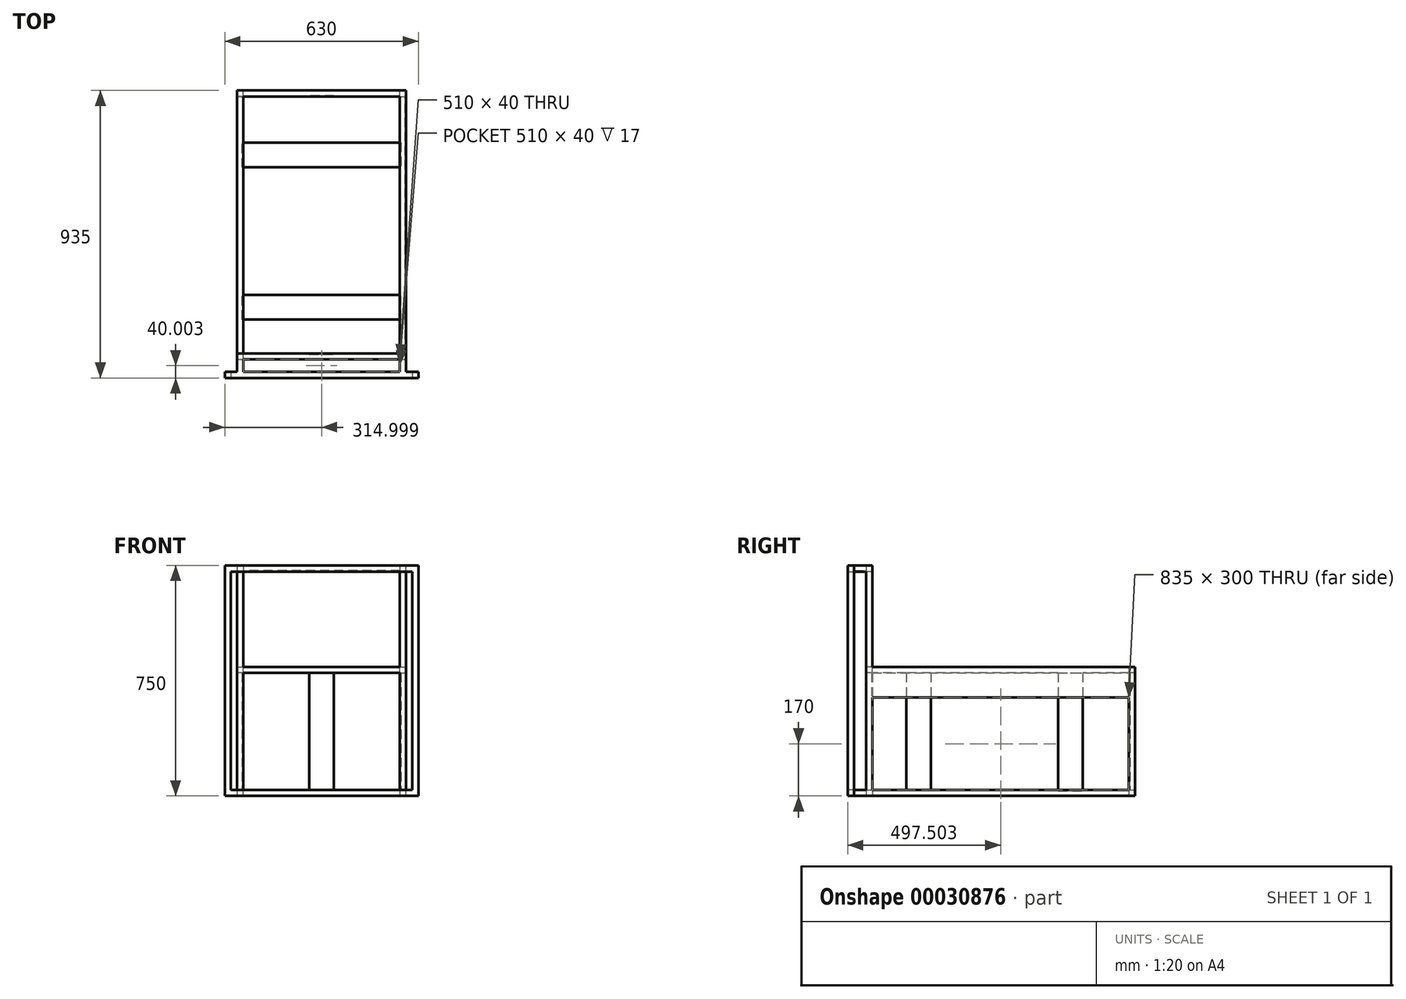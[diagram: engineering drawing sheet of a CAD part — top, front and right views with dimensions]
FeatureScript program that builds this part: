
annotation { "Feature Type Name" : "Feature", "Feature Type Description" : "" }
export const myFeature = defineFeature(function(context is Context, id is Id, definition is map)
    precondition{}
    {
        {
            var Q0;
            Q0=qCreatedBy(makeId("Top.planeOp"),FACE);
            var sketch = newSketch(context, id + "F0", { "sketchPlane" : qUnion([Q0])});
            skLineSegment(sketch, "E0.bottom", {"start": v(-142.85, 483.07) * mm, "end": v(407.15, 483.07) * mm});
            skLineSegment(sketch, "E0.top", {"start": v(-142.85, -391.93) * mm, "end": v(407.15, -391.93) * mm});
            skLineSegment(sketch, "E0.left", {"start": v(-142.85, 483.07) * mm, "end": v(-142.85, -391.93) * mm});
            skLineSegment(sketch, "E0.right", {"start": v(407.15, 483.07) * mm, "end": v(407.15, -391.93) * mm});
            skSolve(sketch);
        }
        {
            var Q0;
            Q0 = qSketchRegion(id + "F0", true);
            extrude(context, id + "F1", {"entities" : qUnion([Q0]), "depth" : 20 * mm});
        }
        {
            var Q0;
            Q0=makeQuery(id+"F1.opExtrude","CAP_FACE",FACE,{"disambiguationData":[OSD([sQuery(id+"F0.wireOp",EDGE,"E0.bottom"),sQuery(id+"F0.wireOp",EDGE,"E0.top"),sQuery(id+"F0.wireOp",EDGE,"E0.left"),sQuery(id+"F0.wireOp",EDGE,"E0.right")])],"isStart":true});
            var sketch = newSketch(context, id + "F2", { "sketchPlane" : qUnion([Q0])});
            skLineSegment(sketch, "E1.bottom", {"start": v(-122.85, 371.93) * mm, "end": v(387.15, 371.93) * mm});
            skLineSegment(sketch, "E1.top", {"start": v(-122.85, -463.07) * mm, "end": v(387.15, -463.07) * mm});
            skLineSegment(sketch, "E1.left", {"start": v(-122.85, 371.93) * mm, "end": v(-122.85, -463.07) * mm});
            skLineSegment(sketch, "E1.right", {"start": v(387.15, 371.93) * mm, "end": v(387.15, -463.07) * mm});
            skSolve(sketch);
        }
        {
            var Q0;
            Q0 = qSketchRegion(id + "F2", true);
            extrude(context, id + "F3", {"entities" : qUnion([Q0]), "operationType" : NewBodyOperationType.REMOVE, "endBound" : BoundingType.THROUGH_ALL, "oppositeDirection" : true, "depth" : 21 * mm});
        }
        {
            var Q0;
            Q0=makeQuery(id+"F3.boolean.opBoolean","COPY",FACE,{"derivedFrom":makeQuery(id+"F3.opExtrude","SWEPT_FACE",FACE,{"disambiguationData":[OSD([sQuery(id+"F2.wireOp",EDGE,"E1.left")])]})});
            var sketch = newSketch(context, id + "F4", { "sketchPlane" : qUnion([Q0])});
            skLineSegment(sketch, "E2.bottom", {"start": v(313.07, 20) * mm, "end": v(233.07, 20) * mm});
            skLineSegment(sketch, "E2.top", {"start": v(313.07, 17) * mm, "end": v(233.07, 17) * mm});
            skLineSegment(sketch, "E2.left", {"start": v(313.07, 20) * mm, "end": v(313.07, 17) * mm});
            skLineSegment(sketch, "E2.right", {"start": v(233.07, 20) * mm, "end": v(233.07, 17) * mm});
            skLineSegment(sketch, "E3.bottom", {"start": v(-261.93, 20) * mm, "end": v(-181.93, 20) * mm});
            skLineSegment(sketch, "E3.top", {"start": v(-261.93, 17) * mm, "end": v(-181.93, 17) * mm});
            skLineSegment(sketch, "E3.left", {"start": v(-261.93, 20) * mm, "end": v(-261.93, 17) * mm});
            skLineSegment(sketch, "E3.right", {"start": v(-181.93, 20) * mm, "end": v(-181.93, 17) * mm});
            skSolve(sketch);
        }
        {
            var Q0;
            Q0 = qSketchRegion(id + "F4", true);
            extrude(context, id + "F5", {"entities" : qUnion([Q0]), "operationType" : NewBodyOperationType.ADD, "endBound" : BoundingType.UP_TO_NEXT, "depth" : 25 * mm});
        }
        {
            var Q0;
            Q0=makeQuery(id+"F5.boolean.opBoolean","MERGE",FACE,{"derivedFrom":[makeQuery(id+"F1.opExtrude","CAP_FACE",FACE,{"disambiguationData":[OSD([sQuery(id+"F0.wireOp",EDGE,"E0.bottom"),sQuery(id+"F0.wireOp",EDGE,"E0.top"),sQuery(id+"F0.wireOp",EDGE,"E0.left"),sQuery(id+"F0.wireOp",EDGE,"E0.right")])],"isStart":false}),makeQuery(id+"F5.opExtrude","SWEPT_FACE",FACE,{"disambiguationData":[OSD([sQuery(id+"F4.wireOp",EDGE,"70eb4137-1e62-4804-9132-5afcea929224.bottom")])]}),makeQuery(id+"F5.opExtrude","SWEPT_FACE",FACE,{"disambiguationData":[OSD([sQuery(id+"F4.wireOp",EDGE,"E2.bottom")])]})]});
            var sketch = newSketch(context, id + "F6", { "sketchPlane" : qUnion([Q0])});
            skLineSegment(sketch, "E4.bottom", {"start": v(-142.85, -391.93) * mm, "end": v(-122.85, -391.93) * mm});
            skLineSegment(sketch, "E4.top", {"start": v(-142.85, -371.93) * mm, "end": v(-122.85, -371.93) * mm});
            skLineSegment(sketch, "E4.left", {"start": v(-142.85, -391.93) * mm, "end": v(-142.85, -371.93) * mm});
            skLineSegment(sketch, "E4.right", {"start": v(-122.85, -391.93) * mm, "end": v(-122.85, -371.93) * mm});
            skLineSegment(sketch, "E5.bottom", {"start": v(407.15, -391.93) * mm, "end": v(387.15, -391.93) * mm});
            skLineSegment(sketch, "E5.top", {"start": v(407.15, -371.93) * mm, "end": v(387.15, -371.93) * mm});
            skLineSegment(sketch, "E5.left", {"start": v(407.15, -391.93) * mm, "end": v(407.15, -371.93) * mm});
            skLineSegment(sketch, "E5.right", {"start": v(387.15, -391.93) * mm, "end": v(387.15, -371.93) * mm});
            skLineSegment(sketch, "E6.bottom", {"start": v(-122.85, 463.07) * mm, "end": v(-142.85, 463.07) * mm});
            skLineSegment(sketch, "E6.top", {"start": v(-122.85, 483.07) * mm, "end": v(-142.85, 483.07) * mm});
            skLineSegment(sketch, "E6.left", {"start": v(-122.85, 463.07) * mm, "end": v(-122.85, 483.07) * mm});
            skLineSegment(sketch, "E6.right", {"start": v(-142.85, 463.07) * mm, "end": v(-142.85, 483.07) * mm});
            skLineSegment(sketch, "E7.bottom", {"start": v(387.15, 463.07) * mm, "end": v(407.15, 463.07) * mm});
            skLineSegment(sketch, "E7.top", {"start": v(387.15, 483.07) * mm, "end": v(407.15, 483.07) * mm});
            skLineSegment(sketch, "E7.left", {"start": v(387.15, 463.07) * mm, "end": v(387.15, 483.07) * mm});
            skLineSegment(sketch, "E7.right", {"start": v(407.15, 463.07) * mm, "end": v(407.15, 483.07) * mm});
            skSolve(sketch);
        }
        {
            var Q0;
            Q0 = qSketchRegion(id + "F6", true);
            extrude(context, id + "F7", {"entities" : qUnion([Q0]), "depth" : 400 * mm});
        }
        {
            var Q0;
            Q0=makeQuery(id+"F7.opExtrude","SWEPT_FACE",FACE,{"disambiguationData":[OSD([sQuery(id+"F6.wireOp",EDGE,"E5.top")])]});
            var sketch = newSketch(context, id + "F8", { "sketchPlane" : qUnion([Q0])});
            skLineSegment(sketch, "E8.bottom", {"start": v(-387.15, 420) * mm, "end": v(-407.15, 420) * mm});
            skLineSegment(sketch, "E8.top", {"start": v(-387.15, 400) * mm, "end": v(-407.15, 400) * mm});
            skLineSegment(sketch, "E8.left", {"start": v(-387.15, 420) * mm, "end": v(-387.15, 400) * mm});
            skLineSegment(sketch, "E8.right", {"start": v(-407.15, 420) * mm, "end": v(-407.15, 400) * mm});
            skSolve(sketch);
        }
        {
            var Q0;
            Q0 = qSketchRegion(id + "F8", true);
            extrude(context, id + "F9", {"entities" : qUnion([Q0]), "operationType" : NewBodyOperationType.ADD, "endBound" : BoundingType.UP_TO_NEXT, "depth" : 25 * mm});
        }
        {
            var Q0;
            Q0=makeQuery(id+"F7.opExtrude","SWEPT_FACE",FACE,{"disambiguationData":[OSD([sQuery(id+"F6.wireOp",EDGE,"E6.bottom")])]});
            var sketch = newSketch(context, id + "F10", { "sketchPlane" : qUnion([Q0])});
            skLineSegment(sketch, "E9.bottom", {"start": v(-142.85, 420) * mm, "end": v(-122.85, 420) * mm});
            skLineSegment(sketch, "E9.top", {"start": v(-142.85, 400) * mm, "end": v(-122.85, 400) * mm});
            skLineSegment(sketch, "E9.left", {"start": v(-142.85, 420) * mm, "end": v(-142.85, 400) * mm});
            skLineSegment(sketch, "E9.right", {"start": v(-122.85, 420) * mm, "end": v(-122.85, 400) * mm});
            skSolve(sketch);
        }
        {
            var Q0;
            Q0 = qSketchRegion(id + "F10", true);
            extrude(context, id + "F11", {"entities" : qUnion([Q0]), "operationType" : NewBodyOperationType.ADD, "endBound" : BoundingType.UP_TO_NEXT, "depth" : 25 * mm});
        }
        {
            var Q0;
            Q0=makeQuery(id+"F9.boolean.opBoolean","MERGE",FACE,{"derivedFrom":[makeQuery(id+"F7.opExtrude","SWEPT_FACE",FACE,{"disambiguationData":[OSD([sQuery(id+"F6.wireOp",EDGE,"E5.right")])]}),makeQuery(id+"F7.opExtrude","SWEPT_FACE",FACE,{"disambiguationData":[OSD([sQuery(id+"F6.wireOp",EDGE,"E7.left")])]}),makeQuery(id+"F9.opExtrude","SWEPT_FACE",FACE,{"disambiguationData":[OSD([sQuery(id+"F8.wireOp",EDGE,"E8.left")])]})]});
            var sketch = newSketch(context, id + "F12", { "sketchPlane" : qUnion([Q0])});
            skLineSegment(sketch, "E10.bottom", {"start": v(371.93, 400) * mm, "end": v(391.93, 400) * mm});
            skLineSegment(sketch, "E10.top", {"start": v(371.93, 420) * mm, "end": v(391.93, 420) * mm});
            skLineSegment(sketch, "E10.left", {"start": v(371.93, 400) * mm, "end": v(371.93, 420) * mm});
            skLineSegment(sketch, "E10.right", {"start": v(391.93, 400) * mm, "end": v(391.93, 420) * mm});
            skSolve(sketch);
        }
        {
            var Q0;
            Q0 = qSketchRegion(id + "F12", true);
            extrude(context, id + "F13", {"entities" : qUnion([Q0]), "operationType" : NewBodyOperationType.ADD, "endBound" : BoundingType.UP_TO_NEXT, "depth" : 25 * mm});
        }
        {
            var Q0;
            Q0=makeQuery(id+"F5.boolean.opBoolean","MERGE",FACE,{"derivedFrom":[makeQuery(id+"F1.opExtrude","CAP_FACE",FACE,{"disambiguationData":[OSD([sQuery(id+"F0.wireOp",EDGE,"E0.bottom"),sQuery(id+"F0.wireOp",EDGE,"E0.top"),sQuery(id+"F0.wireOp",EDGE,"E0.left"),sQuery(id+"F0.wireOp",EDGE,"E0.right")])],"isStart":false}),makeQuery(id+"F5.opExtrude","SWEPT_FACE",FACE,{"disambiguationData":[OSD([sQuery(id+"F4.wireOp",EDGE,"70eb4137-1e62-4804-9132-5afcea929224.bottom")])]}),makeQuery(id+"F5.opExtrude","SWEPT_FACE",FACE,{"disambiguationData":[OSD([sQuery(id+"F4.wireOp",EDGE,"E2.bottom")])]})]});
            var sketch = newSketch(context, id + "F14", { "sketchPlane" : qUnion([Q0])});
            skLineSegment(sketch, "E11.bottom", {"start": v(92.15, -371.93) * mm, "end": v(172.15, -371.93) * mm});
            skLineSegment(sketch, "E11.top", {"start": v(92.15, -374.93) * mm, "end": v(172.15, -374.93) * mm});
            skLineSegment(sketch, "E11.left", {"start": v(92.15, -371.93) * mm, "end": v(92.15, -374.93) * mm});
            skLineSegment(sketch, "E11.right", {"start": v(172.15, -371.93) * mm, "end": v(172.15, -374.93) * mm});
            skLineSegment(sketch, "E12.bottom", {"start": v(172.15, 463.07) * mm, "end": v(92.15, 463.07) * mm});
            skLineSegment(sketch, "E12.top", {"start": v(172.15, 466.07) * mm, "end": v(92.15, 466.07) * mm});
            skLineSegment(sketch, "E12.left", {"start": v(172.15, 463.07) * mm, "end": v(172.15, 466.07) * mm});
            skLineSegment(sketch, "E12.right", {"start": v(92.15, 463.07) * mm, "end": v(92.15, 466.07) * mm});
            skLineSegment(sketch, "E13.bottom", {"start": v(387.15, 313.07) * mm, "end": v(390.15, 313.07) * mm});
            skLineSegment(sketch, "E13.top", {"start": v(387.15, 233.07) * mm, "end": v(390.15, 233.07) * mm});
            skLineSegment(sketch, "E13.left", {"start": v(387.15, 313.07) * mm, "end": v(387.15, 233.07) * mm});
            skLineSegment(sketch, "E13.right", {"start": v(390.15, 313.07) * mm, "end": v(390.15, 233.07) * mm});
            skLineSegment(sketch, "E14.bottom", {"start": v(387.15, -261.93) * mm, "end": v(390.15, -261.93) * mm});
            skLineSegment(sketch, "E14.top", {"start": v(387.15, -181.93) * mm, "end": v(390.15, -181.93) * mm});
            skLineSegment(sketch, "E14.left", {"start": v(387.15, -261.93) * mm, "end": v(387.15, -181.93) * mm});
            skLineSegment(sketch, "E14.right", {"start": v(390.15, -261.93) * mm, "end": v(390.15, -181.93) * mm});
            skLineSegment(sketch, "E15.bottom", {"start": v(-122.85, -261.93) * mm, "end": v(-125.85, -261.93) * mm});
            skLineSegment(sketch, "E15.top", {"start": v(-122.85, -181.93) * mm, "end": v(-125.85, -181.93) * mm});
            skLineSegment(sketch, "E15.left", {"start": v(-122.85, -261.93) * mm, "end": v(-122.85, -181.93) * mm});
            skLineSegment(sketch, "E15.right", {"start": v(-125.85, -261.93) * mm, "end": v(-125.85, -181.93) * mm});
            skLineSegment(sketch, "E16.bottom", {"start": v(-122.85, 233.07) * mm, "end": v(-125.85, 233.07) * mm});
            skLineSegment(sketch, "E16.top", {"start": v(-122.85, 313.07) * mm, "end": v(-125.85, 313.07) * mm});
            skLineSegment(sketch, "E16.left", {"start": v(-122.85, 233.07) * mm, "end": v(-122.85, 313.07) * mm});
            skLineSegment(sketch, "E16.right", {"start": v(-125.85, 233.07) * mm, "end": v(-125.85, 313.07) * mm});
            skSolve(sketch);
        }
        {
            var Q0;
            Q0=makeQuery(id+"F7.opExtrude","SWEPT_FACE",FACE,{"disambiguationData":[OSD([sQuery(id+"F6.wireOp",EDGE,"E7.bottom")])]});
            var sketch = newSketch(context, id + "F15", { "sketchPlane" : qUnion([Q0])});
            skLineSegment(sketch, "E17.bottom", {"start": v(404.15, 400) * mm, "end": v(407.15, 400) * mm});
            skLineSegment(sketch, "E17.top", {"start": v(404.15, 320) * mm, "end": v(407.15, 320) * mm});
            skLineSegment(sketch, "E17.left", {"start": v(404.15, 400) * mm, "end": v(404.15, 320) * mm});
            skLineSegment(sketch, "E17.right", {"start": v(407.15, 400) * mm, "end": v(407.15, 320) * mm});
            skSolve(sketch);
        }
        {
            var Q0;
            Q0 = qSketchRegion(id + "F15", true);
            extrude(context, id + "F16", {"entities" : qUnion([Q0]), "operationType" : NewBodyOperationType.ADD, "endBound" : BoundingType.UP_TO_NEXT, "depth" : 25 * mm});
        }
        {
            var Q0;
            Q0=makeQuery(id+"F7.opExtrude","SWEPT_FACE",FACE,{"disambiguationData":[OSD([sQuery(id+"F6.wireOp",EDGE,"E6.bottom")])]});
            var sketch = newSketch(context, id + "F17", { "sketchPlane" : qUnion([Q0])});
            skLineSegment(sketch, "E18.bottom", {"start": v(-139.85, 400) * mm, "end": v(-142.85, 400) * mm});
            skLineSegment(sketch, "E18.top", {"start": v(-139.85, 320) * mm, "end": v(-142.85, 320) * mm});
            skLineSegment(sketch, "E18.left", {"start": v(-139.85, 400) * mm, "end": v(-139.85, 320) * mm});
            skLineSegment(sketch, "E18.right", {"start": v(-142.85, 400) * mm, "end": v(-142.85, 320) * mm});
            skSolve(sketch);
        }
        {
            var Q0;
            Q0 = qSketchRegion(id + "F17", true);
            extrude(context, id + "F18", {"entities" : qUnion([Q0]), "operationType" : NewBodyOperationType.ADD, "endBound" : BoundingType.UP_TO_NEXT, "depth" : 25 * mm});
        }
        {
            var Q0;
            {var subQ0=sQuery(id+"F6.wireOp",EDGE,"E5.right");var subQ1=makeQuery(id+"F7.opExtrude","SWEPT_FACE",FACE,{"disambiguationData":[OSD([subQ0])]});var subQ2=sQuery(id+"F6.wireOp",EDGE,"E7.left");var subQ3=makeQuery(id+"F7.opExtrude","SWEPT_FACE",FACE,{"disambiguationData":[OSD([subQ2])]});var subQ4=makeQuery(id+"F9.opExtrude","SWEPT_FACE",FACE,{"disambiguationData":[OSD([sQuery(id+"F8.wireOp",EDGE,"E8.left")])]});var subQ5=sQuery(id+"F6.wireOp",EDGE,"E7.bottom");Q0=makeQuery(id+"F13.boolean.opBoolean","SPLIT",FACE,{"disambiguationData":[TD([makeQuery(id+"F7.opExtrude","SWEPT_FACE",FACE,{"disambiguationData":[OSD([subQ5])]})])],"derivedFrom":makeQuery(id+"F9.boolean.opBoolean","MERGE",FACE,{"derivedFrom":[subQ1,subQ3,subQ4]})});}
            var sketch = newSketch(context, id + "F19", { "sketchPlane" : qUnion([Q0])});
            skLineSegment(sketch, "E19.bottom", {"start": v(-483.07, 420) * mm, "end": v(-463.07, 420) * mm});
            skLineSegment(sketch, "E19.top", {"start": v(-483.07, 400) * mm, "end": v(-463.07, 400) * mm});
            skLineSegment(sketch, "E19.left", {"start": v(-483.07, 420) * mm, "end": v(-483.07, 400) * mm});
            skLineSegment(sketch, "E19.right", {"start": v(-463.07, 420) * mm, "end": v(-463.07, 400) * mm});
            skSolve(sketch);
        }
        {
            var Q0;
            Q0 = qSketchRegion(id + "F19", true);
            extrude(context, id + "F20", {"entities" : qUnion([Q0]), "operationType" : NewBodyOperationType.ADD, "endBound" : BoundingType.UP_TO_NEXT, "depth" : 25 * mm});
        }
        {
            var Q0;
            Q0 = qSketchRegion(id + "F14", true);
            extrude(context, id + "F21", {"entities" : qUnion([Q0]), "operationType" : NewBodyOperationType.ADD, "endBound" : BoundingType.UP_TO_NEXT, "depth" : 25 * mm});
        }
        {
            var Q0;
            Q0 = qSketchRegion(id + "F14", true);
            extrude(context, id + "F22", {"entities" : qUnion([Q0]), "operationType" : NewBodyOperationType.ADD, "endBound" : BoundingType.UP_TO_NEXT, "depth" : 25 * mm});
        }
        {
            var Q0;
            Q0=makeQuery(id+"F20.boolean.opBoolean","MERGE",FACE,{"derivedFrom":[makeQuery(id+"F13.boolean.opBoolean","MERGE",FACE,{"derivedFrom":[makeQuery(id+"F9.boolean.opBoolean","MERGE",FACE,{"derivedFrom":[makeQuery(id+"F7.opExtrude","CAP_FACE",FACE,{"disambiguationData":[OSD([sQuery(id+"F6.wireOp",EDGE,"E5.bottom"),sQuery(id+"F6.wireOp",EDGE,"E5.top"),sQuery(id+"F6.wireOp",EDGE,"E5.left"),sQuery(id+"F6.wireOp",EDGE,"E5.right")])],"isStart":false}),makeQuery(id+"F7.opExtrude","CAP_FACE",FACE,{"disambiguationData":[OSD([sQuery(id+"F6.wireOp",EDGE,"E7.bottom"),sQuery(id+"F6.wireOp",EDGE,"E7.top"),sQuery(id+"F6.wireOp",EDGE,"E7.left"),sQuery(id+"F6.wireOp",EDGE,"E7.right")])],"isStart":false}),makeQuery(id+"F9.opExtrude","SWEPT_FACE",FACE,{"disambiguationData":[OSD([sQuery(id+"F8.wireOp",EDGE,"E8.bottom")])]})]}),makeQuery(id+"F11.boolean.opBoolean","MERGE",FACE,{"derivedFrom":[makeQuery(id+"F7.opExtrude","CAP_FACE",FACE,{"disambiguationData":[OSD([sQuery(id+"F6.wireOp",EDGE,"E4.bottom"),sQuery(id+"F6.wireOp",EDGE,"E4.top"),sQuery(id+"F6.wireOp",EDGE,"E4.left"),sQuery(id+"F6.wireOp",EDGE,"E4.right")])],"isStart":false}),makeQuery(id+"F7.opExtrude","CAP_FACE",FACE,{"disambiguationData":[OSD([sQuery(id+"F6.wireOp",EDGE,"E6.bottom"),sQuery(id+"F6.wireOp",EDGE,"E6.top"),sQuery(id+"F6.wireOp",EDGE,"E6.left"),sQuery(id+"F6.wireOp",EDGE,"E6.right")])],"isStart":false}),makeQuery(id+"F11.opExtrude","SWEPT_FACE",FACE,{"disambiguationData":[OSD([sQuery(id+"F10.wireOp",EDGE,"E9.bottom")])]})]}),makeQuery(id+"F13.opExtrude","SWEPT_FACE",FACE,{"disambiguationData":[OSD([sQuery(id+"F12.wireOp",EDGE,"E10.top")])]})]}),makeQuery(id+"F20.opExtrude","SWEPT_FACE",FACE,{"disambiguationData":[OSD([sQuery(id+"F19.wireOp",EDGE,"E19.bottom")])]})]});
            var sketch = newSketch(context, id + "F23", { "sketchPlane" : qUnion([Q0])});
            skLineSegment(sketch, "E20.bottom", {"start": v(-142.85, -391.93) * mm, "end": v(-122.85, -391.93) * mm});
            skLineSegment(sketch, "E20.top", {"start": v(-142.85, -371.93) * mm, "end": v(-122.85, -371.93) * mm});
            skLineSegment(sketch, "E20.left", {"start": v(-142.85, -391.93) * mm, "end": v(-142.85, -371.93) * mm});
            skLineSegment(sketch, "E20.right", {"start": v(-122.85, -391.93) * mm, "end": v(-122.85, -371.93) * mm});
            skLineSegment(sketch, "E21.bottom", {"start": v(387.15, -371.93) * mm, "end": v(407.15, -371.93) * mm});
            skLineSegment(sketch, "E21.top", {"start": v(387.15, -391.93) * mm, "end": v(407.15, -391.93) * mm});
            skLineSegment(sketch, "E21.left", {"start": v(387.15, -371.93) * mm, "end": v(387.15, -391.93) * mm});
            skLineSegment(sketch, "E21.right", {"start": v(407.15, -371.93) * mm, "end": v(407.15, -391.93) * mm});
            skSolve(sketch);
        }
        {
            var Q0;
            Q0 = qSketchRegion(id + "F23", true);
            extrude(context, id + "F24", {"entities" : qUnion([Q0]), "operationType" : NewBodyOperationType.ADD, "depth" : 330 * mm});
        }
        {
            var Q0;
            Q0=makeQuery(id+"F24.opExtrude","SWEPT_FACE",FACE,{"disambiguationData":[OSD([sQuery(id+"F23.wireOp",EDGE,"E21.left")])]});
            var sketch = newSketch(context, id + "F25", { "sketchPlane" : qUnion([Q0])});
            skLineSegment(sketch, "E22.bottom", {"start": v(371.93, 750) * mm, "end": v(391.93, 750) * mm});
            skLineSegment(sketch, "E22.top", {"start": v(371.93, 730) * mm, "end": v(391.93, 730) * mm});
            skLineSegment(sketch, "E22.left", {"start": v(371.93, 750) * mm, "end": v(371.93, 730) * mm});
            skLineSegment(sketch, "E22.right", {"start": v(391.93, 750) * mm, "end": v(391.93, 730) * mm});
            skSolve(sketch);
        }
        {
            var Q0;
            Q0 = qSketchRegion(id + "F25", true);
            extrude(context, id + "F26", {"entities" : qUnion([Q0]), "operationType" : NewBodyOperationType.ADD, "endBound" : BoundingType.UP_TO_NEXT, "depth" : 25 * mm});
        }
        {
            var Q0;
            Q0=makeQuery(id+"F26.boolean.opBoolean","MERGE",FACE,{"derivedFrom":[makeQuery(id+"F24.boolean.opBoolean","MERGE",FACE,{"derivedFrom":[makeQuery(id+"F21.boolean.opBoolean","MERGE",FACE,{"derivedFrom":[makeQuery(id+"F1.opExtrude","SWEPT_FACE",FACE,{"disambiguationData":[OSD([sQuery(id+"F0.wireOp",EDGE,"E0.top")])]}),makeQuery(id+"F13.boolean.opBoolean","MERGE",FACE,{"derivedFrom":[makeQuery(id+"F7.opExtrude","SWEPT_FACE",FACE,{"disambiguationData":[OSD([sQuery(id+"F6.wireOp",EDGE,"E4.bottom")])]}),makeQuery(id+"F7.opExtrude","SWEPT_FACE",FACE,{"disambiguationData":[OSD([sQuery(id+"F6.wireOp",EDGE,"E5.bottom")])]}),makeQuery(id+"F13.opExtrude","SWEPT_FACE",FACE,{"disambiguationData":[OSD([sQuery(id+"F12.wireOp",EDGE,"E10.right")])]})]})]}),makeQuery(id+"F24.opExtrude","SWEPT_FACE",FACE,{"disambiguationData":[OSD([sQuery(id+"F23.wireOp",EDGE,"E20.bottom")])]}),makeQuery(id+"F24.opExtrude","SWEPT_FACE",FACE,{"disambiguationData":[OSD([sQuery(id+"F23.wireOp",EDGE,"E21.top")])]})]}),makeQuery(id+"F26.opExtrude","SWEPT_FACE",FACE,{"disambiguationData":[OSD([sQuery(id+"F25.wireOp",EDGE,"E22.right")])]})]});
            var sketch = newSketch(context, id + "F27", { "sketchPlane" : qUnion([Q0])});
            skLineSegment(sketch, "E23.bottom", {"start": v(-142.85, 0) * mm, "end": v(-122.85, 0) * mm});
            skLineSegment(sketch, "E23.top", {"start": v(-142.85, 20) * mm, "end": v(-122.85, 20) * mm});
            skLineSegment(sketch, "E23.left", {"start": v(-142.85, 0) * mm, "end": v(-142.85, 20) * mm});
            skLineSegment(sketch, "E23.right", {"start": v(-122.85, 0) * mm, "end": v(-122.85, 20) * mm});
            skLineSegment(sketch, "E24.bottom", {"start": v(387.15, 20) * mm, "end": v(407.15, 20) * mm});
            skLineSegment(sketch, "E24.top", {"start": v(387.15, 0) * mm, "end": v(407.15, 0) * mm});
            skLineSegment(sketch, "E24.left", {"start": v(387.15, 20) * mm, "end": v(387.15, 0) * mm});
            skLineSegment(sketch, "E24.right", {"start": v(407.15, 20) * mm, "end": v(407.15, 0) * mm});
            skLineSegment(sketch, "E25.bottom", {"start": v(-142.85, 750) * mm, "end": v(-122.85, 750) * mm});
            skLineSegment(sketch, "E25.top", {"start": v(-142.85, 730) * mm, "end": v(-122.85, 730) * mm});
            skLineSegment(sketch, "E25.left", {"start": v(-142.85, 750) * mm, "end": v(-142.85, 730) * mm});
            skLineSegment(sketch, "E25.right", {"start": v(-122.85, 750) * mm, "end": v(-122.85, 730) * mm});
            skLineSegment(sketch, "E26.bottom", {"start": v(407.15, 750) * mm, "end": v(387.15, 750) * mm});
            skLineSegment(sketch, "E26.top", {"start": v(407.15, 730) * mm, "end": v(387.15, 730) * mm});
            skLineSegment(sketch, "E26.left", {"start": v(407.15, 750) * mm, "end": v(407.15, 730) * mm});
            skLineSegment(sketch, "E26.right", {"start": v(387.15, 750) * mm, "end": v(387.15, 730) * mm});
            skSolve(sketch);
        }
        {
            var Q0;
            Q0 = qSketchRegion(id + "F27", true);
            extrude(context, id + "F28", {"entities" : qUnion([Q0]), "operationType" : NewBodyOperationType.ADD, "depth" : 60 * mm});
        }
        {
            var Q0;
            Q0=makeQuery(id+"F28.opExtrude","SWEPT_FACE",FACE,{"disambiguationData":[OSD([sQuery(id+"F27.wireOp",EDGE,"E25.right")])]});
            var sketch = newSketch(context, id + "F29", { "sketchPlane" : qUnion([Q0])});
            skLineSegment(sketch, "E27.bottom", {"start": v(-451.93, 750) * mm, "end": v(-431.93, 750) * mm});
            skLineSegment(sketch, "E27.top", {"start": v(-451.93, 730) * mm, "end": v(-431.93, 730) * mm});
            skLineSegment(sketch, "E27.left", {"start": v(-451.93, 750) * mm, "end": v(-451.93, 730) * mm});
            skLineSegment(sketch, "E27.right", {"start": v(-431.93, 750) * mm, "end": v(-431.93, 730) * mm});
            skSolve(sketch);
        }
        {
            var Q0;
            Q0 = qSketchRegion(id + "F29", true);
            extrude(context, id + "F30", {"entities" : qUnion([Q0]), "operationType" : NewBodyOperationType.ADD, "endBound" : BoundingType.UP_TO_NEXT, "depth" : 25 * mm});
        }
        {
            var Q0;
            Q0=makeQuery(id+"F28.opExtrude","SWEPT_FACE",FACE,{"disambiguationData":[OSD([sQuery(id+"F27.wireOp",EDGE,"E24.left")])]});
            var sketch = newSketch(context, id + "F31", { "sketchPlane" : qUnion([Q0])});
            skLineSegment(sketch, "E28.bottom", {"start": v(451.93, 20) * mm, "end": v(431.93, 20) * mm});
            skLineSegment(sketch, "E28.top", {"start": v(451.93, 0) * mm, "end": v(431.93, 0) * mm});
            skLineSegment(sketch, "E28.left", {"start": v(451.93, 20) * mm, "end": v(451.93, 0) * mm});
            skLineSegment(sketch, "E28.right", {"start": v(431.93, 20) * mm, "end": v(431.93, 0) * mm});
            skSolve(sketch);
        }
        {
            var Q0;
            Q0 = qSketchRegion(id + "F31", true);
            extrude(context, id + "F32", {"entities" : qUnion([Q0]), "operationType" : NewBodyOperationType.ADD, "endBound" : BoundingType.UP_TO_NEXT, "depth" : 25 * mm});
        }
        {
            var Q0;
            Q0=makeQuery(id+"F28.boolean.opBoolean","MERGE",FACE,{"derivedFrom":[makeQuery(id+"F24.boolean.opBoolean","MERGE",FACE,{"derivedFrom":[makeQuery(id+"F21.boolean.opBoolean","MERGE",FACE,{"derivedFrom":[makeQuery(id+"F1.opExtrude","SWEPT_FACE",FACE,{"disambiguationData":[OSD([sQuery(id+"F0.wireOp",EDGE,"E0.left")])]}),makeQuery(id+"F18.boolean.opBoolean","MERGE",FACE,{"derivedFrom":[makeQuery(id+"F11.boolean.opBoolean","MERGE",FACE,{"derivedFrom":[makeQuery(id+"F7.opExtrude","SWEPT_FACE",FACE,{"disambiguationData":[OSD([sQuery(id+"F6.wireOp",EDGE,"E4.left")])]}),makeQuery(id+"F7.opExtrude","SWEPT_FACE",FACE,{"disambiguationData":[OSD([sQuery(id+"F6.wireOp",EDGE,"E6.right")])]}),makeQuery(id+"F11.opExtrude","SWEPT_FACE",FACE,{"disambiguationData":[OSD([sQuery(id+"F10.wireOp",EDGE,"E9.left")])]})]}),makeQuery(id+"F18.opExtrude","SWEPT_FACE",FACE,{"disambiguationData":[OSD([sQuery(id+"F17.wireOp",EDGE,"E18.right")])]})]})]}),makeQuery(id+"F24.opExtrude","SWEPT_FACE",FACE,{"disambiguationData":[OSD([sQuery(id+"F23.wireOp",EDGE,"E20.left")])]})]}),makeQuery(id+"F28.opExtrude","SWEPT_FACE",FACE,{"disambiguationData":[OSD([sQuery(id+"F27.wireOp",EDGE,"E23.left")])]}),makeQuery(id+"F28.opExtrude","SWEPT_FACE",FACE,{"disambiguationData":[OSD([sQuery(id+"F27.wireOp",EDGE,"E25.left")])]})]});
            var sketch = newSketch(context, id + "F33", { "sketchPlane" : qUnion([Q0])});
            skLineSegment(sketch, "E29.bottom", {"start": v(451.93, 20) * mm, "end": v(431.93, 20) * mm});
            skLineSegment(sketch, "E29.top", {"start": v(451.93, 0) * mm, "end": v(431.93, 0) * mm});
            skLineSegment(sketch, "E29.left", {"start": v(451.93, 20) * mm, "end": v(451.93, 0) * mm});
            skLineSegment(sketch, "E29.right", {"start": v(431.93, 20) * mm, "end": v(431.93, 0) * mm});
            skLineSegment(sketch, "E30.bottom", {"start": v(451.93, 750) * mm, "end": v(431.93, 750) * mm});
            skLineSegment(sketch, "E30.top", {"start": v(451.93, 730) * mm, "end": v(431.93, 730) * mm});
            skLineSegment(sketch, "E30.left", {"start": v(451.93, 750) * mm, "end": v(451.93, 730) * mm});
            skLineSegment(sketch, "E30.right", {"start": v(431.93, 750) * mm, "end": v(431.93, 730) * mm});
            skSolve(sketch);
        }
        {
            var Q0;
            Q0 = qSketchRegion(id + "F33", true);
            extrude(context, id + "F34", {"entities" : qUnion([Q0]), "operationType" : NewBodyOperationType.ADD, "depth" : 40 * mm});
        }
        {
            var Q0;
            Q0=makeQuery(id+"F28.boolean.opBoolean","MERGE",FACE,{"derivedFrom":[makeQuery(id+"F24.boolean.opBoolean","MERGE",FACE,{"derivedFrom":[makeQuery(id+"F21.boolean.opBoolean","MERGE",FACE,{"derivedFrom":[makeQuery(id+"F1.opExtrude","SWEPT_FACE",FACE,{"disambiguationData":[OSD([sQuery(id+"F0.wireOp",EDGE,"E0.right")])]}),makeQuery(id+"F16.boolean.opBoolean","MERGE",FACE,{"derivedFrom":[makeQuery(id+"F9.boolean.opBoolean","MERGE",FACE,{"derivedFrom":[makeQuery(id+"F7.opExtrude","SWEPT_FACE",FACE,{"disambiguationData":[OSD([sQuery(id+"F6.wireOp",EDGE,"E5.left")])]}),makeQuery(id+"F7.opExtrude","SWEPT_FACE",FACE,{"disambiguationData":[OSD([sQuery(id+"F6.wireOp",EDGE,"E7.right")])]}),makeQuery(id+"F9.opExtrude","SWEPT_FACE",FACE,{"disambiguationData":[OSD([sQuery(id+"F8.wireOp",EDGE,"E8.right")])]})]}),makeQuery(id+"F16.opExtrude","SWEPT_FACE",FACE,{"disambiguationData":[OSD([sQuery(id+"F15.wireOp",EDGE,"E17.right")])]})]})]}),makeQuery(id+"F24.opExtrude","SWEPT_FACE",FACE,{"disambiguationData":[OSD([sQuery(id+"F23.wireOp",EDGE,"E21.right")])]})]}),makeQuery(id+"F28.opExtrude","SWEPT_FACE",FACE,{"disambiguationData":[OSD([sQuery(id+"F27.wireOp",EDGE,"E24.right")])]}),makeQuery(id+"F28.opExtrude","SWEPT_FACE",FACE,{"disambiguationData":[OSD([sQuery(id+"F27.wireOp",EDGE,"E26.left")])]})]});
            var sketch = newSketch(context, id + "F35", { "sketchPlane" : qUnion([Q0])});
            skLineSegment(sketch, "E31.bottom", {"start": v(-451.93, 0) * mm, "end": v(-431.93, 0) * mm});
            skLineSegment(sketch, "E31.top", {"start": v(-451.93, 20) * mm, "end": v(-431.93, 20) * mm});
            skLineSegment(sketch, "E31.left", {"start": v(-451.93, 0) * mm, "end": v(-451.93, 20) * mm});
            skLineSegment(sketch, "E31.right", {"start": v(-431.93, 0) * mm, "end": v(-431.93, 20) * mm});
            skLineSegment(sketch, "E32.bottom", {"start": v(-451.93, 730) * mm, "end": v(-431.93, 730) * mm});
            skLineSegment(sketch, "E32.top", {"start": v(-451.93, 750) * mm, "end": v(-431.93, 750) * mm});
            skLineSegment(sketch, "E32.left", {"start": v(-451.93, 730) * mm, "end": v(-451.93, 750) * mm});
            skLineSegment(sketch, "E32.right", {"start": v(-431.93, 730) * mm, "end": v(-431.93, 750) * mm});
            skSolve(sketch);
        }
        {
            var Q0;
            Q0 = qSketchRegion(id + "F35", true);
            extrude(context, id + "F36", {"entities" : qUnion([Q0]), "operationType" : NewBodyOperationType.ADD, "depth" : 40 * mm});
        }
        {
            var Q0;
            Q0=makeQuery(id+"F36.boolean.opBoolean","MERGE",FACE,{"derivedFrom":[makeQuery(id+"F34.boolean.opBoolean","MERGE",FACE,{"derivedFrom":[makeQuery(id+"F30.boolean.opBoolean","MERGE",FACE,{"derivedFrom":[makeQuery(id+"F28.opExtrude","SWEPT_FACE",FACE,{"disambiguationData":[OSD([sQuery(id+"F27.wireOp",EDGE,"E25.top")])]}),makeQuery(id+"F28.opExtrude","SWEPT_FACE",FACE,{"disambiguationData":[OSD([sQuery(id+"F27.wireOp",EDGE,"E26.top")])]}),makeQuery(id+"F30.opExtrude","SWEPT_FACE",FACE,{"disambiguationData":[OSD([sQuery(id+"F29.wireOp",EDGE,"E27.top")])]})]}),makeQuery(id+"F34.opExtrude","SWEPT_FACE",FACE,{"disambiguationData":[OSD([sQuery(id+"F33.wireOp",EDGE,"E30.top")])]})]}),makeQuery(id+"F36.opExtrude","SWEPT_FACE",FACE,{"disambiguationData":[OSD([sQuery(id+"F35.wireOp",EDGE,"E32.bottom")])]})]});
            var sketch = newSketch(context, id + "F37", { "sketchPlane" : qUnion([Q0])});
            skLineSegment(sketch, "E33.bottom", {"start": v(427.15, 451.93) * mm, "end": v(447.15, 451.93) * mm});
            skLineSegment(sketch, "E33.top", {"start": v(427.15, 431.93) * mm, "end": v(447.15, 431.93) * mm});
            skLineSegment(sketch, "E33.left", {"start": v(427.15, 451.93) * mm, "end": v(427.15, 431.93) * mm});
            skLineSegment(sketch, "E33.right", {"start": v(447.15, 451.93) * mm, "end": v(447.15, 431.93) * mm});
            skLineSegment(sketch, "E34.bottom", {"start": v(-162.85, 451.93) * mm, "end": v(-182.85, 451.93) * mm});
            skLineSegment(sketch, "E34.top", {"start": v(-162.85, 431.93) * mm, "end": v(-182.85, 431.93) * mm});
            skLineSegment(sketch, "E34.left", {"start": v(-162.85, 451.93) * mm, "end": v(-162.85, 431.93) * mm});
            skLineSegment(sketch, "E34.right", {"start": v(-182.85, 451.93) * mm, "end": v(-182.85, 431.93) * mm});
            skSolve(sketch);
        }
        {
            var Q0;
            Q0 = qSketchRegion(id + "F37", true);
            extrude(context, id + "F38", {"entities" : qUnion([Q0]), "operationType" : NewBodyOperationType.ADD, "endBound" : BoundingType.UP_TO_NEXT, "depth" : 25 * mm});
        }
        {
            var Q0;
            {var subQ0=makeQuery(id+"F1.opExtrude","SWEPT_FACE",FACE,{"disambiguationData":[OSD([sQuery(id+"F0.wireOp",EDGE,"E0.top")])]});var subQ1=makeQuery(id+"F7.opExtrude","SWEPT_FACE",FACE,{"disambiguationData":[OSD([sQuery(id+"F6.wireOp",EDGE,"E4.bottom")])]});var subQ2=makeQuery(id+"F7.opExtrude","SWEPT_FACE",FACE,{"disambiguationData":[OSD([sQuery(id+"F6.wireOp",EDGE,"E5.bottom")])]});var subQ3=makeQuery(id+"F13.opExtrude","SWEPT_FACE",FACE,{"disambiguationData":[OSD([sQuery(id+"F12.wireOp",EDGE,"E10.right")])]});var subQ4=sQuery(id+"F23.wireOp",EDGE,"E20.bottom");var subQ5=makeQuery(id+"F24.opExtrude","SWEPT_FACE",FACE,{"disambiguationData":[OSD([subQ4])]});var subQ6=sQuery(id+"F23.wireOp",EDGE,"E21.top");var subQ7=makeQuery(id+"F24.opExtrude","SWEPT_FACE",FACE,{"disambiguationData":[OSD([subQ6])]});var subQ8=makeQuery(id+"F26.opExtrude","SWEPT_FACE",FACE,{"disambiguationData":[OSD([sQuery(id+"F25.wireOp",EDGE,"E22.right")])]});Q0=makeQuery(id+"F28.boolean.opBoolean","SPLIT",FACE,{"disambiguationData":[TD([makeQuery(id+"F26.opExtrude","SWEPT_FACE",FACE,{"disambiguationData":[OSD([sQuery(id+"F25.wireOp",EDGE,"E22.bottom")])]})])],"derivedFrom":makeQuery(id+"F26.boolean.opBoolean","MERGE",FACE,{"derivedFrom":[makeQuery(id+"F24.boolean.opBoolean","MERGE",FACE,{"derivedFrom":[makeQuery(id+"F21.boolean.opBoolean","MERGE",FACE,{"derivedFrom":[subQ0,makeQuery(id+"F13.boolean.opBoolean","MERGE",FACE,{"derivedFrom":[subQ1,subQ2,subQ3]})]}),subQ5,subQ7]}),subQ8]})});}
            var sketch = newSketch(context, id + "F39", { "sketchPlane" : qUnion([Q0])});
            skLineSegment(sketch, "E35.bottom", {"start": v(-122.85, 733) * mm, "end": v(114.3, 733) * mm});
            skLineSegment(sketch, "E35.top", {"start": v(-122.85, 730) * mm, "end": v(114.3, 730) * mm});
            skLineSegment(sketch, "E35.left", {"start": v(-122.85, 733) * mm, "end": v(-122.85, 730) * mm});
            skLineSegment(sketch, "E36.bottom", {"start": v(114.3, 733) * mm, "end": v(387.15, 733) * mm});
            skLineSegment(sketch, "E36.top", {"start": v(114.3, 730) * mm, "end": v(387.15, 730) * mm});
            skLineSegment(sketch, "E36.right", {"start": v(387.15, 733) * mm, "end": v(387.15, 730) * mm});
            skSolve(sketch);
        }
        {
            var Q0;
            Q0 = qSketchRegion(id + "F39", true);
            extrude(context, id + "F40", {"entities" : qUnion([Q0]), "operationType" : NewBodyOperationType.ADD, "endBound" : BoundingType.UP_TO_NEXT, "depth" : 25 * mm});
        }
    });
